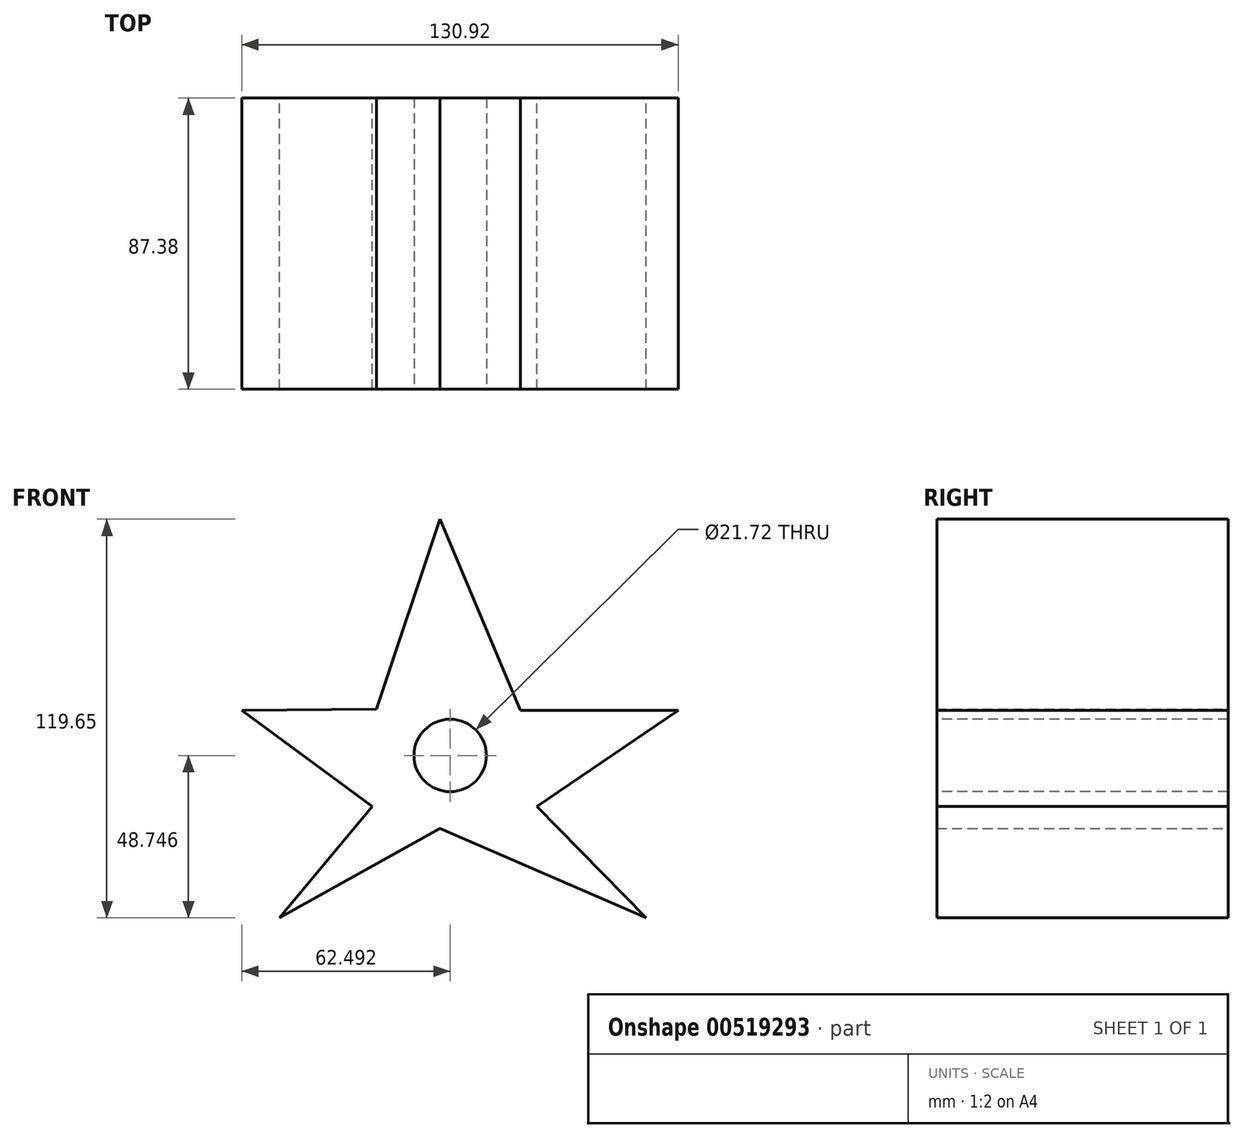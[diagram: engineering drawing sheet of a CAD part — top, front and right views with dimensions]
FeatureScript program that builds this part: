
annotation { "Feature Type Name" : "Feature", "Feature Type Description" : "" }
export const myFeature = defineFeature(function(context is Context, id is Id, definition is map)
    precondition{}
    {
        {
            var Q0;
            Q0=qCreatedBy(makeId("Front.planeOp"),FACE);
            var sketch = newSketch(context, id + "F0", { "sketchPlane" : qUnion([Q0])});
            skLineSegment(sketch, "E0", {"start": v(-18.98, 20.13) * mm, "end": v(0, 77.14) * mm});
            skLineSegment(sketch, "E1", {"start": v(0, 77.14) * mm, "end": v(24.1, 19.8) * mm});
            skLineSegment(sketch, "E2", {"start": v(24.1, 19.8) * mm, "end": v(71.5, 19.8) * mm});
            skLineSegment(sketch, "E3", {"start": v(71.5, 19.8) * mm, "end": v(29.07, -9.04) * mm});
            skLineSegment(sketch, "E4", {"start": v(29.07, -9.04) * mm, "end": v(61.89, -42.51) * mm});
            skLineSegment(sketch, "E5", {"start": v(61.89, -42.51) * mm, "end": v(0, -15.66) * mm});
            skLineSegment(sketch, "E6", {"start": v(0, -15.66) * mm, "end": v(-48.15, -42.51) * mm});
            skLineSegment(sketch, "E7", {"start": v(-48.15, -42.51) * mm, "end": v(-20.3, -9.04) * mm});
            skLineSegment(sketch, "E8", {"start": v(-20.3, -9.04) * mm, "end": v(-59.42, 19.8) * mm});
            skLineSegment(sketch, "E9", {"start": v(-59.42, 19.8) * mm, "end": v(-18.98, 20.13) * mm});
            skSolve(sketch);
        }
        {
            var Q0;
            Q0=makeQuery(id+"F0.imprint","IMPRINT",FACE,{"disambiguationData":[TD([[makeQuery(id+"F0.imprint","IMPRINT",EDGE,{"derivedFrom":sQuery(id+"F0.wireOp",EDGE,"E0")}),-1.0]])]});
            extrude(context, id + "F1", {"entities" : qUnion([Q0]), "endBound" : BoundingType.SYMMETRIC, "depth" : 87.38 * mm, "offsetDistance" : 25.4 * mm});
        }
        {
            var Q0;
            Q0=makeQuery(id+"F1.opExtrude","CAP_FACE",FACE,{"disambiguationData":[OSD([sQuery(id+"F0.wireOp",EDGE,"E0"),sQuery(id+"F0.wireOp",EDGE,"E1"),sQuery(id+"F0.wireOp",EDGE,"E2"),sQuery(id+"F0.wireOp",EDGE,"E3"),sQuery(id+"F0.wireOp",EDGE,"E4"),sQuery(id+"F0.wireOp",EDGE,"E5"),sQuery(id+"F0.wireOp",EDGE,"E6"),sQuery(id+"F0.wireOp",EDGE,"E7"),sQuery(id+"F0.wireOp",EDGE,"E8"),sQuery(id+"F0.wireOp",EDGE,"E9")])],"isStart":false});
            var sketch = newSketch(context, id + "F2", { "sketchPlane" : qUnion([Q0])});
            skCircle(sketch, "E10", {"center": v(3.07, 6.24) * mm, "radius": 10.86 * mm});
            skSolve(sketch);
        }
        {
            var Q0;
            Q0=makeQuery(id+"F2.imprint","IMPRINT",FACE,{"disambiguationData":[TD([[makeQuery(id+"F2.imprint","IMPRINT",EDGE,{"derivedFrom":sQuery(id+"F2.wireOp",EDGE,"E10")}),1.0]])]});
            extrude(context, id + "F3", {"entities" : qUnion([Q0]), "operationType" : NewBodyOperationType.REMOVE, "endBound" : BoundingType.THROUGH_ALL, "oppositeDirection" : true, "depth" : 25.4 * mm, "offsetDistance" : 25.4 * mm});
        }
    });
